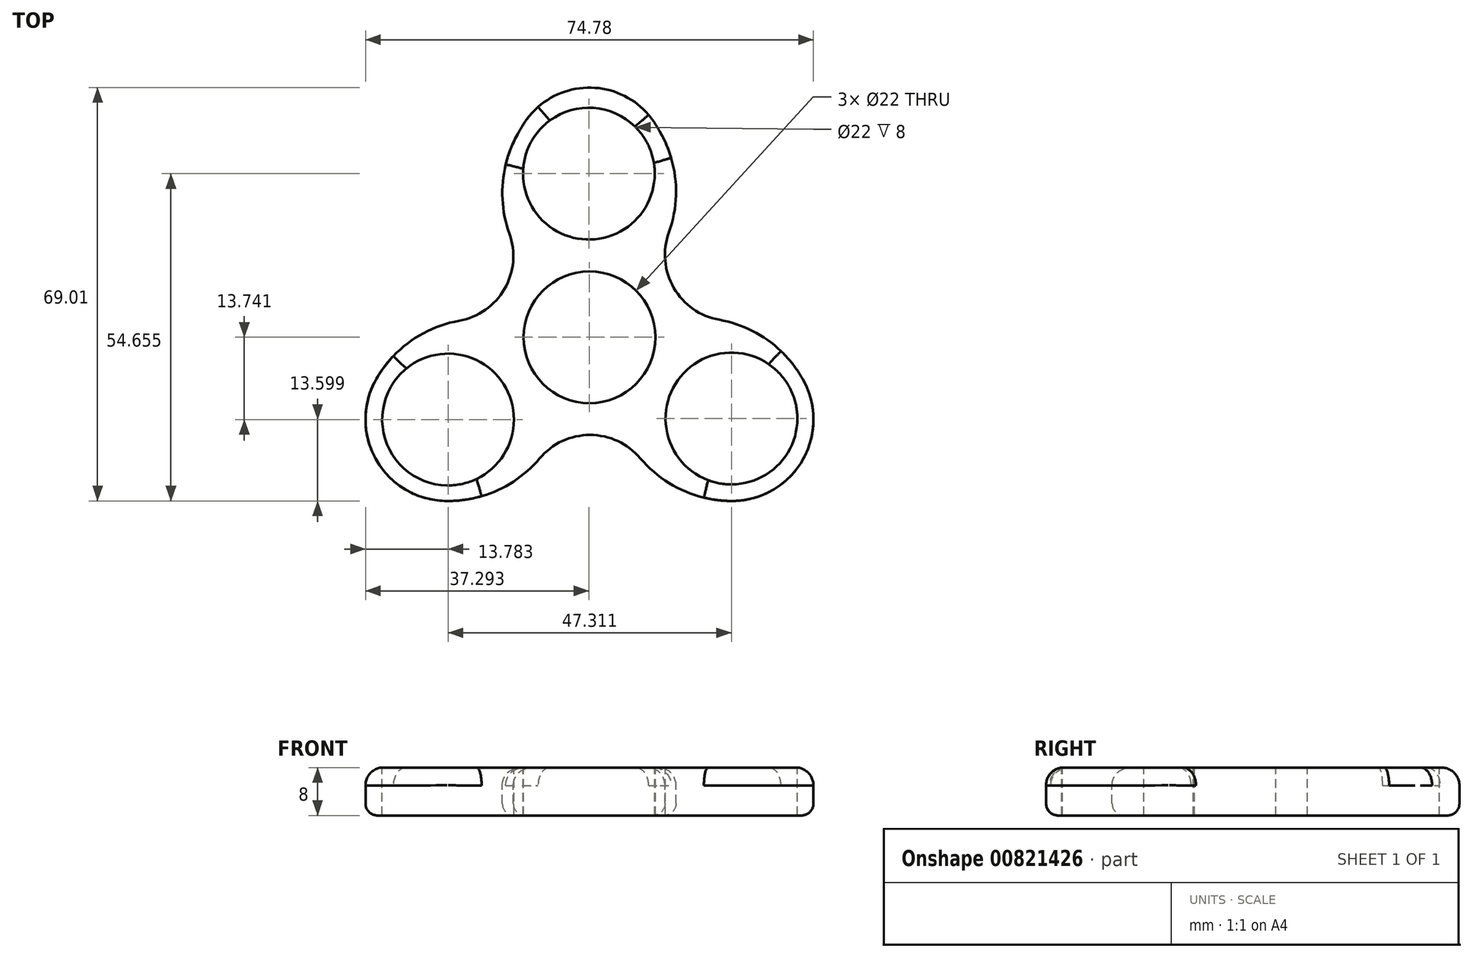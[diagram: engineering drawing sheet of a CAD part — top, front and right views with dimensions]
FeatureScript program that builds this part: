
annotation { "Feature Type Name" : "Feature", "Feature Type Description" : "" }
export const myFeature = defineFeature(function(context is Context, id is Id, definition is map)
    precondition{}
    {
        {
            var Q0;
            Q0=qCreatedBy(makeId("Top.planeOp"),FACE);
            var sketch = newSketch(context, id + "F0", { "sketchPlane" : qUnion([Q0])});
            skCircle(sketch, "E0.cCircle", {"center": v(0, 0) * mm, "radius": 23.66 * mm, "construction": true});
            skPoint(sketch, "E0.0.midPoint", {"position": v(11.9, -20.44) * mm});
            skCircle(sketch, "E1", {"center": v(-0.1, 27.31) * mm, "radius": 11 * mm});
            skCircle(sketch, "E2", {"center": v(-23.7, 13.57) * mm, "radius": 11 * mm});
            skCircle(sketch, "E3", {"center": v(-23.6, -13.74) * mm, "radius": 11 * mm});
            skCircle(sketch, "E4", {"center": v(0.1, -27.31) * mm, "radius": 11 * mm});
            skCircle(sketch, "E5", {"center": v(23.7, -13.57) * mm, "radius": 11 * mm});
            skCircle(sketch, "E6", {"center": v(23.6, 13.74) * mm, "radius": 11 * mm});
            skCircle(sketch, "E7", {"center": v(0, 0) * mm, "radius": 11 * mm});
            skSolve(sketch);
        }
        {
            var Q0;
            Q0=qCreatedBy(makeId("Top.planeOp"),FACE);
            var sketch = newSketch(context, id + "F1", { "sketchPlane" : qUnion([Q0])});
            skCircle(sketch, "E8.cCircle", {"center": v(0, 0) * mm, "radius": 27.34 * mm, "construction": true});
            skLineSegment(sketch, "E8.0", {"start": v(47.35, -27.34) * mm, "end": v(-47.35, -27.34) * mm});
            skLineSegment(sketch, "E8.1", {"start": v(-47.35, -27.34) * mm, "end": v(0, 54.67) * mm});
            skLineSegment(sketch, "E8.2", {"start": v(0, 54.67) * mm, "end": v(47.35, -27.34) * mm});
            skPoint(sketch, "E8.0.midPoint", {"position": v(0, -27.34) * mm});
            skSolve(sketch);
        }
        {
            var Q0;
            Q0=makeQuery(id+"F1.imprint","IMPRINT",FACE,{"disambiguationData":[TD([[makeQuery(id+"F1.imprint","IMPRINT",EDGE,{"derivedFrom":sQuery(id+"F1.wireOp",EDGE,"E8.0")}),-1.0]])]});
            extrude(context, id + "F2", {"entities" : qUnion([Q0]), "oppositeDirection" : true, "depth" : 8 * mm, "offsetDistance" : 25 * mm});
        }
        {
            var Q0;
            Q0=makeQuery(id+"F0.imprint","IMPRINT",FACE,{"disambiguationData":[TD([[makeQuery(id+"F0.imprint","IMPRINT",EDGE,{"derivedFrom":sQuery(id+"F0.wireOp",EDGE,"E4")}),1.0]])]});
            var Q1;
            Q1=makeQuery(id+"F0.imprint","IMPRINT",FACE,{"disambiguationData":[TD([[makeQuery(id+"F0.imprint","IMPRINT",EDGE,{"derivedFrom":sQuery(id+"F0.wireOp",EDGE,"E3")}),1.0]])]});
            var Q2;
            Q2=makeQuery(id+"F0.imprint","IMPRINT",FACE,{"disambiguationData":[TD([[makeQuery(id+"F0.imprint","IMPRINT",EDGE,{"derivedFrom":sQuery(id+"F0.wireOp",EDGE,"E2")}),1.0]])]});
            var Q3;
            Q3=makeQuery(id+"F0.imprint","IMPRINT",FACE,{"disambiguationData":[TD([[makeQuery(id+"F0.imprint","IMPRINT",EDGE,{"derivedFrom":sQuery(id+"F0.wireOp",EDGE,"E7")}),1.0]])]});
            var Q4;
            Q4=makeQuery(id+"F0.imprint","IMPRINT",FACE,{"disambiguationData":[TD([[makeQuery(id+"F0.imprint","IMPRINT",EDGE,{"derivedFrom":sQuery(id+"F0.wireOp",EDGE,"E1")}),1.0]])]});
            var Q5;
            Q5=makeQuery(id+"F0.imprint","IMPRINT",FACE,{"disambiguationData":[TD([[makeQuery(id+"F0.imprint","IMPRINT",EDGE,{"derivedFrom":sQuery(id+"F0.wireOp",EDGE,"E6")}),1.0]])]});
            var Q6;
            Q6=makeQuery(id+"F0.imprint","IMPRINT",FACE,{"disambiguationData":[TD([[makeQuery(id+"F0.imprint","IMPRINT",EDGE,{"derivedFrom":sQuery(id+"F0.wireOp",EDGE,"E5")}),1.0]])]});
            extrude(context, id + "F3", {"entities" : qUnion([Q0, Q1, Q2, Q3, Q4, Q5, Q6]), "operationType" : NewBodyOperationType.REMOVE, "oppositeDirection" : true, "depth" : 25 * mm, "offsetDistance" : 25 * mm});
        }
        {
            var Q0;
            Q0=makeQuery(id+"F2.opExtrude","SWEPT_EDGE",EDGE,{"disambiguationData":[OSD([sQuery(id+"F1.wireOp",EDGE,"E8.1"),sQuery(id+"F1.wireOp",EDGE,"E8.2")])]});
            fillet(context, id + "F4", {"entities" : qUnion([Q0]), "radius" : 13 * mm, "tangentPropagation" : true, "allowEdgeOverflow" : false});
        }
        {
            var Q0;
            Q0=makeQuery(id+"F2.opExtrude","SWEPT_EDGE",EDGE,{"disambiguationData":[OSD([sQuery(id+"F1.wireOp",EDGE,"E8.0"),sQuery(id+"F1.wireOp",EDGE,"E8.2")])]});
            fillet(context, id + "F5", {"entities" : qUnion([Q0]), "radius" : 13.6 * mm, "tangentPropagation" : true, "allowEdgeOverflow" : false});
        }
        {
            var Q0;
            Q0=makeQuery(id+"F2.opExtrude","SWEPT_EDGE",EDGE,{"disambiguationData":[OSD([sQuery(id+"F1.wireOp",EDGE,"E8.0"),sQuery(id+"F1.wireOp",EDGE,"E8.1")])]});
            fillet(context, id + "F6", {"entities" : qUnion([Q0]), "radius" : 13.6 * mm, "tangentPropagation" : true, "allowEdgeOverflow" : false});
        }
        {
            var Q0;
            Q0=makeQuery(id+"F3.boolean.opBoolean","INTERSECT",EDGE,{"disambiguationData":[OD(1.0)],"derivedFrom":[makeQuery(id+"F2.opExtrude","SWEPT_FACE",FACE,{"disambiguationData":[OSD([sQuery(id+"F1.wireOp",EDGE,"E8.2")])]}),makeQuery(id+"F3.opExtrude","SWEPT_FACE",FACE,{"disambiguationData":[OSD([sQuery(id+"F0.wireOp",EDGE,"E6")])]})]});
            var Q1;
            Q1=makeQuery(id+"F3.boolean.opBoolean","INTERSECT",EDGE,{"disambiguationData":[OD(0.0)],"derivedFrom":[makeQuery(id+"F2.opExtrude","SWEPT_FACE",FACE,{"disambiguationData":[OSD([sQuery(id+"F1.wireOp",EDGE,"E8.2")])]}),makeQuery(id+"F3.opExtrude","SWEPT_FACE",FACE,{"disambiguationData":[OSD([sQuery(id+"F0.wireOp",EDGE,"E6")])]})]});
            var Q2;
            Q2=makeQuery(id+"F3.boolean.opBoolean","INTERSECT",EDGE,{"disambiguationData":[OD(0.0)],"derivedFrom":[makeQuery(id+"F2.opExtrude","SWEPT_FACE",FACE,{"disambiguationData":[OSD([sQuery(id+"F1.wireOp",EDGE,"E8.0")])]}),makeQuery(id+"F3.opExtrude","SWEPT_FACE",FACE,{"disambiguationData":[OSD([sQuery(id+"F0.wireOp",EDGE,"E4")])]})]});
            var Q3;
            Q3=makeQuery(id+"F3.boolean.opBoolean","INTERSECT",EDGE,{"disambiguationData":[OD(1.0)],"derivedFrom":[makeQuery(id+"F2.opExtrude","SWEPT_FACE",FACE,{"disambiguationData":[OSD([sQuery(id+"F1.wireOp",EDGE,"E8.0")])]}),makeQuery(id+"F3.opExtrude","SWEPT_FACE",FACE,{"disambiguationData":[OSD([sQuery(id+"F0.wireOp",EDGE,"E4")])]})]});
            var Q4;
            Q4=makeQuery(id+"F3.boolean.opBoolean","INTERSECT",EDGE,{"disambiguationData":[OD(1.0)],"derivedFrom":[makeQuery(id+"F2.opExtrude","SWEPT_FACE",FACE,{"disambiguationData":[OSD([sQuery(id+"F1.wireOp",EDGE,"E8.1")])]}),makeQuery(id+"F3.opExtrude","SWEPT_FACE",FACE,{"disambiguationData":[OSD([sQuery(id+"F0.wireOp",EDGE,"E2")])]})]});
            var Q5;
            Q5=makeQuery(id+"F3.boolean.opBoolean","INTERSECT",EDGE,{"disambiguationData":[OD(0.0)],"derivedFrom":[makeQuery(id+"F2.opExtrude","SWEPT_FACE",FACE,{"disambiguationData":[OSD([sQuery(id+"F1.wireOp",EDGE,"E8.1")])]}),makeQuery(id+"F3.opExtrude","SWEPT_FACE",FACE,{"disambiguationData":[OSD([sQuery(id+"F0.wireOp",EDGE,"E2")])]})]});
            fillet(context, id + "F7", {"entities" : qUnion([Q0, Q1, Q2, Q3, Q4, Q5]), "radius" : 20 * mm, "tangentPropagation" : true, "allowEdgeOverflow" : false});
        }
        {
            var Q0;
            Q0=makeQuery(id+"F3.boolean.opBoolean","COPY",EDGE,{"derivedFrom":makeQuery(id+"F3.opExtrude","CAP_EDGE",EDGE,{"disambiguationData":[OSD([sQuery(id+"F0.wireOp",EDGE,"E2")])],"isStart":true})});
            var Q1;
            {var subQ0=sQuery(id+"F1.wireOp",EDGE,"E8.1");Q1=makeQuery(id+"F7.opFillet","BLEND_EDGE",EDGE,{"blendedFrom":[makeQuery(id+"F3.boolean.opBoolean","INTERSECT",EDGE,{"disambiguationData":[OD(1.0)],"derivedFrom":[makeQuery(id+"F2.opExtrude","SWEPT_FACE",FACE,{"disambiguationData":[OSD([subQ0])]}),makeQuery(id+"F3.opExtrude","SWEPT_FACE",FACE,{"disambiguationData":[OSD([sQuery(id+"F0.wireOp",EDGE,"E2")])]})]}),makeQuery(id+"F2.opExtrude","CAP_FACE",FACE,{"disambiguationData":[OSD([sQuery(id+"F1.wireOp",EDGE,"E8.0"),subQ0,sQuery(id+"F1.wireOp",EDGE,"E8.2")])],"isStart":true})],"blendedInto":[makeQuery(id+"F2.opExtrude","CAP_FACE",FACE,{"disambiguationData":[OSD([sQuery(id+"F1.wireOp",EDGE,"E8.0"),subQ0,sQuery(id+"F1.wireOp",EDGE,"E8.2")])],"isStart":true})]});}
            fillet(context, id + "F8", {"entities" : qUnion([Q0, Q1]), "radius" : 3 * mm, "tangentPropagation" : true, "allowEdgeOverflow" : false});
        }
        {
            var Q0;
            {var subQ0=sQuery(id+"F1.wireOp",EDGE,"E8.1");var subQ1=sQuery(id+"F1.wireOp",EDGE,"E8.0");Q0=makeQuery(id+"F6.opFillet","BLEND_EDGE",EDGE,{"blendedFrom":[makeQuery(id+"F2.opExtrude","SWEPT_EDGE",EDGE,{"disambiguationData":[OSD([subQ1,subQ0])]}),makeQuery(id+"F2.opExtrude","CAP_FACE",FACE,{"disambiguationData":[OSD([subQ1,subQ0,sQuery(id+"F1.wireOp",EDGE,"E8.2")])],"isStart":false})],"blendedInto":[makeQuery(id+"F2.opExtrude","CAP_FACE",FACE,{"disambiguationData":[OSD([subQ1,subQ0,sQuery(id+"F1.wireOp",EDGE,"E8.2")])],"isStart":false})]});}
            var Q1;
            {var subQ0=sQuery(id+"F1.wireOp",EDGE,"E8.2");var subQ1=sQuery(id+"F1.wireOp",EDGE,"E8.0");Q1=makeQuery(id+"F5.opFillet","BLEND_EDGE",EDGE,{"blendedFrom":[makeQuery(id+"F2.opExtrude","SWEPT_EDGE",EDGE,{"disambiguationData":[OSD([subQ1,subQ0])]}),makeQuery(id+"F2.opExtrude","CAP_FACE",FACE,{"disambiguationData":[OSD([subQ1,sQuery(id+"F1.wireOp",EDGE,"E8.1"),subQ0])],"isStart":false})],"blendedInto":[makeQuery(id+"F2.opExtrude","CAP_FACE",FACE,{"disambiguationData":[OSD([subQ1,sQuery(id+"F1.wireOp",EDGE,"E8.1"),subQ0])],"isStart":false})]});}
            var Q2;
            {var subQ0=sQuery(id+"F1.wireOp",EDGE,"E8.2");var subQ1=sQuery(id+"F1.wireOp",EDGE,"E8.1");Q2=makeQuery(id+"F4.opFillet","BLEND_EDGE",EDGE,{"blendedFrom":[makeQuery(id+"F2.opExtrude","SWEPT_EDGE",EDGE,{"disambiguationData":[OSD([subQ1,subQ0])]}),makeQuery(id+"F2.opExtrude","CAP_FACE",FACE,{"disambiguationData":[OSD([sQuery(id+"F1.wireOp",EDGE,"E8.0"),subQ1,subQ0])],"isStart":false})],"blendedInto":[makeQuery(id+"F2.opExtrude","CAP_FACE",FACE,{"disambiguationData":[OSD([sQuery(id+"F1.wireOp",EDGE,"E8.0"),subQ1,subQ0])],"isStart":false})]});}
            fillet(context, id + "F9", {"entities" : qUnion([Q0, Q1, Q2]), "radius" : 2 * mm, "tangentPropagation" : true, "allowEdgeOverflow" : false});
        }
    });
